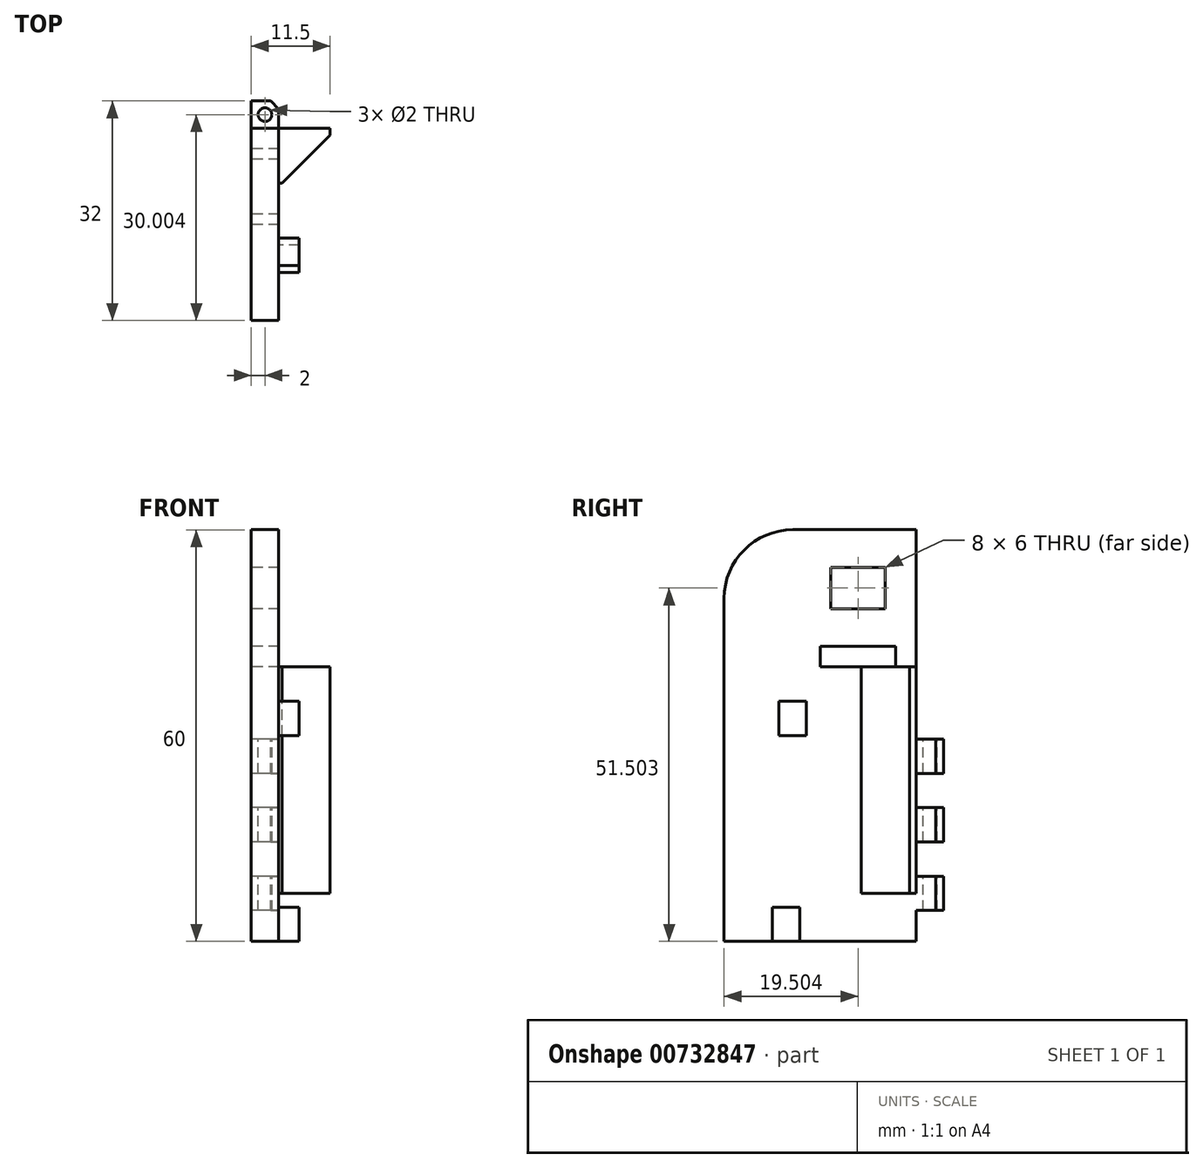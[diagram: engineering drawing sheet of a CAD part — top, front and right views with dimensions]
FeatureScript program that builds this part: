
annotation { "Feature Type Name" : "Feature", "Feature Type Description" : "" }
export const myFeature = defineFeature(function(context is Context, id is Id, definition is map)
    precondition{}
    {
        {
            var Q0;
            Q0=qCreatedBy(makeId("Right.planeOp"),FACE);
            var sketch = newSketch(context, id + "F0", { "sketchPlane" : qUnion([Q0])});
            skLineSegment(sketch, "E0.bottom", {"start": v(39.74, 71.65) * mm, "end": v(11.74, 71.65) * mm});
            skLineSegment(sketch, "E0.top", {"start": v(39.74, 11.65) * mm, "end": v(11.74, 11.65) * mm});
            skLineSegment(sketch, "E0.left", {"start": v(39.74, 71.65) * mm, "end": v(39.74, 11.65) * mm});
            skLineSegment(sketch, "E0.right", {"start": v(11.74, 71.65) * mm, "end": v(11.74, 11.65) * mm});
            skSolve(sketch);
        }
        {
            var Q0;
            Q0=makeQuery(id+"F0.imprint","IMPRINT",FACE,{"disambiguationData":[TD([[makeQuery(id+"F0.imprint","IMPRINT",EDGE,{"derivedFrom":sQuery(id+"F0.wireOp",EDGE,"E0.bottom")}),1.0]])]});
            extrude(context, id + "F1", {"entities" : qUnion([Q0]), "depth" : 4 * mm, "offsetDistance" : 25 * mm});
        }
        {
            var Q0;
            Q0=makeQuery(id+"F1.opExtrude","CAP_FACE",FACE,{"disambiguationData":[OSD([sQuery(id+"F0.wireOp",EDGE,"E0.bottom"),sQuery(id+"F0.wireOp",EDGE,"E0.top"),sQuery(id+"F0.wireOp",EDGE,"E0.left"),sQuery(id+"F0.wireOp",EDGE,"E0.right")])],"isStart":false});
            var sketch = newSketch(context, id + "F2", { "sketchPlane" : qUnion([Q0])});
            skLineSegment(sketch, "E1.bottom", {"start": v(19.74, 46.65) * mm, "end": v(23.74, 46.65) * mm});
            skLineSegment(sketch, "E1.top", {"start": v(19.74, 41.65) * mm, "end": v(23.74, 41.65) * mm});
            skLineSegment(sketch, "E1.left", {"start": v(19.74, 46.65) * mm, "end": v(19.74, 41.65) * mm});
            skLineSegment(sketch, "E1.right", {"start": v(23.74, 46.65) * mm, "end": v(23.74, 41.65) * mm});
            skLineSegment(sketch, "E2.bottom", {"start": v(18.74, 16.65) * mm, "end": v(22.74, 16.65) * mm});
            skLineSegment(sketch, "E2.top", {"start": v(18.74, 11.65) * mm, "end": v(22.74, 11.65) * mm});
            skLineSegment(sketch, "E2.left", {"start": v(18.74, 16.65) * mm, "end": v(18.74, 11.65) * mm});
            skLineSegment(sketch, "E2.right", {"start": v(22.74, 16.65) * mm, "end": v(22.74, 11.65) * mm});
            skSolve(sketch);
        }
        {
            var Q0;
            Q0=makeQuery(id+"F2.imprint","IMPRINT",FACE,{"disambiguationData":[TD([[makeQuery(id+"F2.imprint","IMPRINT",EDGE,{"derivedFrom":sQuery(id+"F2.wireOp",EDGE,"E1.bottom")}),-1.0]])]});
            var Q1;
            Q1=makeQuery(id+"F2.imprint","IMPRINT",FACE,{"disambiguationData":[TD([[makeQuery(id+"F2.imprint","IMPRINT",EDGE,{"derivedFrom":sQuery(id+"F2.wireOp",EDGE,"E2.bottom")}),-1.0]])]});
            extrude(context, id + "F3", {"entities" : qUnion([Q0, Q1]), "operationType" : NewBodyOperationType.ADD, "depth" : 3 * mm, "offsetDistance" : 25 * mm});
        }
        {
            var Q0;
            Q0=makeQuery(id+"F1.opExtrude","CAP_FACE",FACE,{"disambiguationData":[OSD([sQuery(id+"F0.wireOp",EDGE,"E0.bottom"),sQuery(id+"F0.wireOp",EDGE,"E0.top"),sQuery(id+"F0.wireOp",EDGE,"E0.left"),sQuery(id+"F0.wireOp",EDGE,"E0.right")])],"isStart":true});
            var sketch = newSketch(context, id + "F4", { "sketchPlane" : qUnion([Q0])});
            skLineSegment(sketch, "E3.bottom", {"start": v(-39.74, 26.15) * mm, "end": v(-43.74, 26.15) * mm});
            skLineSegment(sketch, "E3.top", {"start": v(-39.74, 31.15) * mm, "end": v(-43.74, 31.15) * mm});
            skLineSegment(sketch, "E3.left", {"start": v(-39.74, 26.15) * mm, "end": v(-39.74, 31.15) * mm});
            skLineSegment(sketch, "E3.right", {"start": v(-43.74, 26.15) * mm, "end": v(-43.74, 31.15) * mm});
            skLineSegment(sketch, "E4.bottom", {"start": v(-39.74, 36.15) * mm, "end": v(-43.74, 36.15) * mm});
            skLineSegment(sketch, "E4.top", {"start": v(-39.74, 41.15) * mm, "end": v(-43.74, 41.15) * mm});
            skLineSegment(sketch, "E4.left", {"start": v(-39.74, 36.15) * mm, "end": v(-39.74, 41.15) * mm});
            skLineSegment(sketch, "E4.right", {"start": v(-43.74, 36.15) * mm, "end": v(-43.74, 41.15) * mm});
            skLineSegment(sketch, "E5.bottom", {"start": v(-39.74, 21.15) * mm, "end": v(-43.74, 21.15) * mm});
            skLineSegment(sketch, "E5.top", {"start": v(-39.74, 16.15) * mm, "end": v(-43.74, 16.15) * mm});
            skLineSegment(sketch, "E5.left", {"start": v(-39.74, 21.15) * mm, "end": v(-39.74, 16.15) * mm});
            skLineSegment(sketch, "E5.right", {"start": v(-43.74, 21.15) * mm, "end": v(-43.74, 16.15) * mm});
            skSolve(sketch);
        }
        {
            var Q0;
            Q0=makeQuery(id+"F4.imprint","IMPRINT",FACE,{"disambiguationData":[TD([[makeQuery(id+"F4.imprint","IMPRINT",EDGE,{"derivedFrom":sQuery(id+"F4.wireOp",EDGE,"E4.bottom")}),-1.0]])]});
            var Q1;
            Q1=makeQuery(id+"F4.imprint","IMPRINT",FACE,{"disambiguationData":[TD([[makeQuery(id+"F4.imprint","IMPRINT",EDGE,{"derivedFrom":sQuery(id+"F4.wireOp",EDGE,"E3.bottom")}),-1.0]])]});
            var Q2;
            Q2=makeQuery(id+"F4.imprint","IMPRINT",FACE,{"disambiguationData":[TD([[makeQuery(id+"F4.imprint","IMPRINT",EDGE,{"derivedFrom":sQuery(id+"F4.wireOp",EDGE,"E5.bottom")}),1.0]])]});
            extrude(context, id + "F5", {"entities" : qUnion([Q0, Q1, Q2]), "operationType" : NewBodyOperationType.ADD, "depth" : -4 * mm, "offsetDistance" : 25 * mm});
        }
        {
            var Q0;
            Q0=makeQuery(id+"F5.opExtrude","SWEPT_FACE",FACE,{"disambiguationData":[OSD([sQuery(id+"F4.wireOp",EDGE,"E4.top")])]});
            var sketch = newSketch(context, id + "F6", { "sketchPlane" : qUnion([Q0])});
            skCircle(sketch, "E6", {"center": v(2, 41.74) * mm, "radius": 1 * mm});
            skCircle(sketch, "E7.cCircle", {"center": v(2, 41.74) * mm, "radius": 2 * mm, "construction": true});
            skLineSegment(sketch, "E7.0", {"start": v(0, 40.92) * mm, "end": v(0, 42.57) * mm});
            skLineSegment(sketch, "E7.1", {"start": v(0, 42.57) * mm, "end": v(1.17, 43.74) * mm});
            skLineSegment(sketch, "E7.2", {"start": v(1.17, 43.74) * mm, "end": v(2.83, 43.74) * mm});
            skLineSegment(sketch, "E7.3", {"start": v(2.83, 43.74) * mm, "end": v(4, 42.57) * mm});
            skLineSegment(sketch, "E7.4", {"start": v(4, 42.57) * mm, "end": v(4, 40.92) * mm});
            skLineSegment(sketch, "E7.5", {"start": v(4, 40.92) * mm, "end": v(2.83, 39.74) * mm});
            skLineSegment(sketch, "E7.6", {"start": v(2.83, 39.74) * mm, "end": v(1.17, 39.74) * mm});
            skLineSegment(sketch, "E7.7", {"start": v(1.17, 39.74) * mm, "end": v(0, 40.92) * mm});
            skPoint(sketch, "E7.0.midPoint", {"position": v(0, 41.74) * mm});
            skSolve(sketch);
        }
        {
            var Q0;
            Q0=makeQuery(id+"F6.imprint","IMPRINT",FACE,{"disambiguationData":[TD([[makeQuery(id+"F6.imprint","IMPRINT",EDGE,{"derivedFrom":sQuery(id+"F6.wireOp",EDGE,"E6")}),1.0]])]});
            var Q1;
            {var subQ0=sQuery(id+"F6.wireOp",EDGE,"E7.3");Q1=makeQuery(id+"F6.imprint","IMPRINT",FACE,{"disambiguationData":[TD([[makeQuery(id+"F6.imprint","IMPRINT",EDGE,{"derivedFrom":subQ0}),1.0]])]});}
            extrude(context, id + "F7", {"entities" : qUnion([Q0, Q1]), "operationType" : NewBodyOperationType.REMOVE, "oppositeDirection" : true, "depth" : 25 * mm, "offsetDistance" : 25 * mm});
        }
        {
            var Q0;
            Q0=makeQuery(id+"F1.opExtrude","SWEPT_EDGE",EDGE,{"disambiguationData":[OSD([sQuery(id+"F0.wireOp",EDGE,"E0.bottom"),sQuery(id+"F0.wireOp",EDGE,"E0.right")])]});
            fillet(context, id + "F8", {"entities" : qUnion([Q0]), "radius" : 10 * mm, "tangentPropagation" : true, "allowEdgeOverflow" : false});
        }
        {
            var Q0;
            Q0=makeQuery(id+"F5.boolean.opBoolean","MERGE",FACE,{"derivedFrom":[makeQuery(id+"F1.opExtrude","CAP_FACE",FACE,{"disambiguationData":[OSD([sQuery(id+"F0.wireOp",EDGE,"E0.bottom"),sQuery(id+"F0.wireOp",EDGE,"E0.top"),sQuery(id+"F0.wireOp",EDGE,"E0.left"),sQuery(id+"F0.wireOp",EDGE,"E0.right")])],"isStart":true}),makeQuery(id+"F5.opExtrude","CAP_FACE",FACE,{"disambiguationData":[OSD([sQuery(id+"F4.wireOp",EDGE,"E3.bottom"),sQuery(id+"F4.wireOp",EDGE,"E3.top"),sQuery(id+"F4.wireOp",EDGE,"E3.left"),sQuery(id+"F4.wireOp",EDGE,"E3.right")])],"isStart":true}),makeQuery(id+"F5.opExtrude","CAP_FACE",FACE,{"disambiguationData":[OSD([sQuery(id+"F4.wireOp",EDGE,"E4.bottom"),sQuery(id+"F4.wireOp",EDGE,"E4.top"),sQuery(id+"F4.wireOp",EDGE,"E4.left"),sQuery(id+"F4.wireOp",EDGE,"E4.right")])],"isStart":true}),makeQuery(id+"F5.opExtrude","CAP_FACE",FACE,{"disambiguationData":[OSD([sQuery(id+"F4.wireOp",EDGE,"E5.bottom"),sQuery(id+"F4.wireOp",EDGE,"E5.top"),sQuery(id+"F4.wireOp",EDGE,"E5.left"),sQuery(id+"F4.wireOp",EDGE,"E5.right")])],"isStart":true})]});
            var sketch = newSketch(context, id + "F9", { "sketchPlane" : qUnion([Q0])});
            skCircle(sketch, "E8", {"center": v(-31.24, 63.15) * mm, "radius": 5 * mm});
            skCircle(sketch, "E9", {"center": v(-31.24, 63.15) * mm, "radius": 5.5 * mm});
            skLineSegment(sketch, "E10", {"start": v(-35.24, 66.15) * mm, "end": v(-35.24, 60.15) * mm});
            skLineSegment(sketch, "E11", {"start": v(-35.24, 60.15) * mm, "end": v(-27.24, 60.15) * mm});
            skLineSegment(sketch, "E12", {"start": v(-27.24, 60.15) * mm, "end": v(-27.24, 66.15) * mm});
            skLineSegment(sketch, "E13", {"start": v(-27.24, 66.15) * mm, "end": v(-35.24, 66.15) * mm});
            skCircle(sketch, "E14", {"center": v(-31.24, 63.15) * mm, "radius": 1 * mm});
            skLineSegment(sketch, "E15.bottom", {"start": v(-36.74, 54.65) * mm, "end": v(-25.74, 54.65) * mm});
            skLineSegment(sketch, "E15.top", {"start": v(-36.74, 51.65) * mm, "end": v(-25.74, 51.65) * mm});
            skLineSegment(sketch, "E15.left", {"start": v(-36.74, 54.65) * mm, "end": v(-36.74, 51.65) * mm});
            skLineSegment(sketch, "E15.right", {"start": v(-25.74, 54.65) * mm, "end": v(-25.74, 51.65) * mm});
            skSolve(sketch);
        }
        {
            var Q0;
            Q0=makeQuery(id+"F9.imprint","IMPRINT",FACE,{"disambiguationData":[TD([[makeQuery(id+"F9.imprint","IMPRINT",EDGE,{"derivedFrom":sQuery(id+"F9.wireOp",EDGE,"E10")}),1.0]])]});
            var Q1;
            Q1=makeQuery(id+"F9.imprint","IMPRINT",FACE,{"disambiguationData":[TD([[makeQuery(id+"F9.imprint","IMPRINT",EDGE,{"derivedFrom":sQuery(id+"F9.wireOp",EDGE,"E14")}),1.0]])]});
            var Q2;
            Q2=makeQuery(id+"F9.imprint","IMPRINT",FACE,{"disambiguationData":[TD([[makeQuery(id+"F9.imprint","IMPRINT",EDGE,{"derivedFrom":sQuery(id+"F9.wireOp",EDGE,"E15.bottom")}),-1.0]])]});
            extrude(context, id + "F10", {"entities" : qUnion([Q0, Q1, Q2]), "operationType" : NewBodyOperationType.REMOVE, "oppositeDirection" : true, "depth" : 25 * mm, "offsetDistance" : 25 * mm});
        }
        {
            var Q0;
            Q0=makeQuery(id+"F5.boolean.opBoolean","MERGE",FACE,{"derivedFrom":[makeQuery(id+"F1.opExtrude","CAP_FACE",FACE,{"disambiguationData":[OSD([sQuery(id+"F0.wireOp",EDGE,"E0.bottom"),sQuery(id+"F0.wireOp",EDGE,"E0.top"),sQuery(id+"F0.wireOp",EDGE,"E0.left"),sQuery(id+"F0.wireOp",EDGE,"E0.right")])],"isStart":false}),makeQuery(id+"F5.opExtrude","CAP_FACE",FACE,{"disambiguationData":[OSD([sQuery(id+"F4.wireOp",EDGE,"E3.bottom"),sQuery(id+"F4.wireOp",EDGE,"E3.top"),sQuery(id+"F4.wireOp",EDGE,"E3.left"),sQuery(id+"F4.wireOp",EDGE,"E3.right")])],"isStart":false}),makeQuery(id+"F5.opExtrude","CAP_FACE",FACE,{"disambiguationData":[OSD([sQuery(id+"F4.wireOp",EDGE,"E4.bottom"),sQuery(id+"F4.wireOp",EDGE,"E4.top"),sQuery(id+"F4.wireOp",EDGE,"E4.left"),sQuery(id+"F4.wireOp",EDGE,"E4.right")])],"isStart":false}),makeQuery(id+"F5.opExtrude","CAP_FACE",FACE,{"disambiguationData":[OSD([sQuery(id+"F4.wireOp",EDGE,"E5.bottom"),sQuery(id+"F4.wireOp",EDGE,"E5.top"),sQuery(id+"F4.wireOp",EDGE,"E5.left"),sQuery(id+"F4.wireOp",EDGE,"E5.right")])],"isStart":false})]});
            var sketch = newSketch(context, id + "F11", { "sketchPlane" : qUnion([Q0])});
            skLineSegment(sketch, "E16.bottom", {"start": v(39.74, 51.65) * mm, "end": v(31.74, 51.65) * mm});
            skLineSegment(sketch, "E16.top", {"start": v(39.74, 18.65) * mm, "end": v(31.74, 18.65) * mm});
            skLineSegment(sketch, "E16.left", {"start": v(39.74, 51.65) * mm, "end": v(39.74, 18.65) * mm});
            skLineSegment(sketch, "E16.right", {"start": v(31.74, 51.65) * mm, "end": v(31.74, 18.65) * mm});
            skSolve(sketch);
        }
        {
            var Q0;
            {var subQ15=sQuery(id+"F11.wireOp",EDGE,"E16.top");Q0=makeQuery(id+"F11.imprint","IMPRINT",FACE,{"disambiguationData":[TD([[makeQuery(id+"F11.imprint","IMPRINT",EDGE,{"derivedFrom":subQ15}),-1.0]])]});}
            extrude(context, id + "F12", {"entities" : qUnion([Q0]), "operationType" : NewBodyOperationType.ADD, "depth" : 7.5 * mm, "offsetDistance" : 25 * mm});
        }
        {
            var Q0;
            Q0=makeQuery(id+"F12.opExtrude","CAP_EDGE",EDGE,{"disambiguationData":[OSD([sQuery(id+"F11.wireOp",EDGE,"E16.right")])],"isStart":false});
            chamfer(context, id + "F13", {"entities" : qUnion([Q0]), "width" : 7 * mm, "tangentPropagation" : true});
        }
    });
